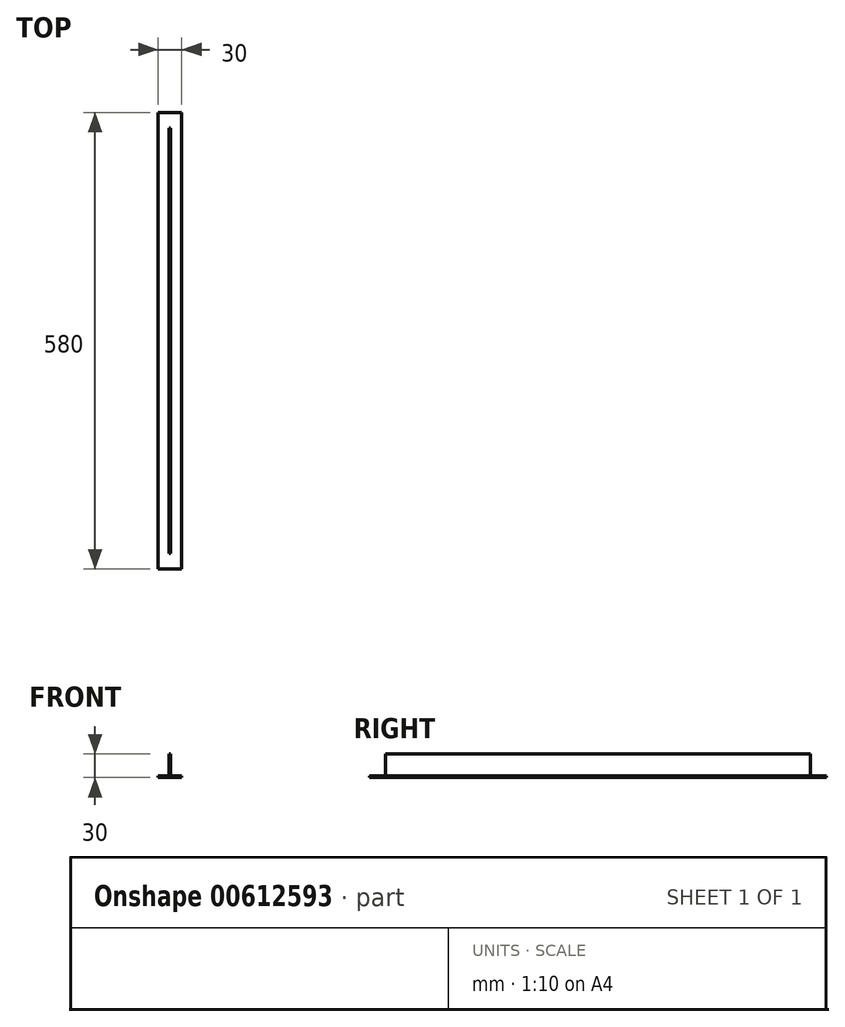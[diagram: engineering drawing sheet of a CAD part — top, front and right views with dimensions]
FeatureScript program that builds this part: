
annotation { "Feature Type Name" : "Feature", "Feature Type Description" : "" }
export const myFeature = defineFeature(function(context is Context, id is Id, definition is map)
    precondition{}
    {
        {
            var Q0;
            Q0=qCreatedBy(makeId("Front.planeOp"),FACE);
            var sketch = newSketch(context, id + "F0", { "sketchPlane" : qUnion([Q0])});
            skLineSegment(sketch, "E0", {"start": v(0, 30) * mm, "end": v(1, 30) * mm});
            skLineSegment(sketch, "E1", {"start": v(1, 30) * mm, "end": v(1, 2) * mm});
            skLineSegment(sketch, "E2", {"start": v(1, 2) * mm, "end": v(15, 2) * mm});
            skLineSegment(sketch, "E3", {"start": v(15, 2) * mm, "end": v(15, 0) * mm});
            skLineSegment(sketch, "E4", {"start": v(15, 0) * mm, "end": v(0, 0) * mm});
            skLineSegment(sketch, "E5", {"start": v(0, 0) * mm, "end": v(0, 30) * mm, "construction": true});
            skLineSegment(sketch, "E6.MirrorCS", {"start": v(0, 30) * mm, "end": v(-1, 30) * mm});
            skLineSegment(sketch, "E7.MirrorCS", {"start": v(-1, 30) * mm, "end": v(-1, 2) * mm});
            skLineSegment(sketch, "E8.MirrorCS", {"start": v(-1, 2) * mm, "end": v(-15, 2) * mm});
            skLineSegment(sketch, "E9.MirrorCS", {"start": v(-15, 2) * mm, "end": v(-15, 0) * mm});
            skLineSegment(sketch, "E10.MirrorCS", {"start": v(-15, 0) * mm, "end": v(0, 0) * mm});
            skSolve(sketch);
        }
        {
            var Q0;
            Q0=makeQuery(id+"F0.imprint","IMPRINT",FACE,{"disambiguationData":[TD([[makeQuery(id+"F0.imprint","IMPRINT",EDGE,{"derivedFrom":sQuery(id+"F0.wireOp",EDGE,"E0")}),-1.0]])]});
            extrude(context, id + "F1", {"entities" : qUnion([Q0]), "depth" : 540 * mm, "offsetDistance" : 25.4 * mm});
        }
        {
            var Q0;
            Q0=makeQuery(id+"F1.opExtrude","CAP_FACE",FACE,{"disambiguationData":[OSD([sQuery(id+"F0.wireOp",EDGE,"E0"),sQuery(id+"F0.wireOp",EDGE,"E1"),sQuery(id+"F0.wireOp",EDGE,"E2"),sQuery(id+"F0.wireOp",EDGE,"E3"),sQuery(id+"F0.wireOp",EDGE,"E4"),sQuery(id+"F0.wireOp",EDGE,"E6.MirrorCS"),sQuery(id+"F0.wireOp",EDGE,"E7.MirrorCS"),sQuery(id+"F0.wireOp",EDGE,"E8.MirrorCS"),sQuery(id+"F0.wireOp",EDGE,"E9.MirrorCS"),sQuery(id+"F0.wireOp",EDGE,"E10.MirrorCS")])],"isStart":false});
            var sketch = newSketch(context, id + "F2", { "sketchPlane" : qUnion([Q0])});
            skLineSegment(sketch, "E11.bottom", {"start": v(-15, 2) * mm, "end": v(15, 2) * mm});
            skLineSegment(sketch, "E11.top", {"start": v(-15, 0) * mm, "end": v(15, 0) * mm});
            skLineSegment(sketch, "E11.left", {"start": v(-15, 2) * mm, "end": v(-15, 0) * mm});
            skLineSegment(sketch, "E11.right", {"start": v(15, 2) * mm, "end": v(15, 0) * mm});
            skSolve(sketch);
        }
        {
            var Q0;
            Q0=makeQuery(id+"F2.imprint","IMPRINT",FACE,{"disambiguationData":[TD([[makeQuery(id+"F2.imprint","IMPRINT",EDGE,{"derivedFrom":sQuery(id+"F2.wireOp",EDGE,"E11.top")}),1.0]])]});
            extrude(context, id + "F3", {"entities" : qUnion([Q0]), "operationType" : NewBodyOperationType.ADD, "depth" : 20 * mm, "offsetDistance" : 25.4 * mm});
        }
        {
            var Q0;
            Q0=makeQuery(id+"F1.opExtrude","CAP_FACE",FACE,{"disambiguationData":[OSD([sQuery(id+"F0.wireOp",EDGE,"E0"),sQuery(id+"F0.wireOp",EDGE,"E1"),sQuery(id+"F0.wireOp",EDGE,"E2"),sQuery(id+"F0.wireOp",EDGE,"E3"),sQuery(id+"F0.wireOp",EDGE,"E4"),sQuery(id+"F0.wireOp",EDGE,"E6.MirrorCS"),sQuery(id+"F0.wireOp",EDGE,"E7.MirrorCS"),sQuery(id+"F0.wireOp",EDGE,"E8.MirrorCS"),sQuery(id+"F0.wireOp",EDGE,"E9.MirrorCS"),sQuery(id+"F0.wireOp",EDGE,"E10.MirrorCS")])],"isStart":true});
            var sketch = newSketch(context, id + "F4", { "sketchPlane" : qUnion([Q0])});
            skLineSegment(sketch, "E12.bottom", {"start": v(-15, 2) * mm, "end": v(15, 2) * mm});
            skLineSegment(sketch, "E12.top", {"start": v(-15, 0) * mm, "end": v(15, 0) * mm});
            skLineSegment(sketch, "E12.left", {"start": v(-15, 2) * mm, "end": v(-15, 0) * mm});
            skLineSegment(sketch, "E12.right", {"start": v(15, 2) * mm, "end": v(15, 0) * mm});
            skSolve(sketch);
        }
        {
            var Q0;
            Q0=makeQuery(id+"F4.imprint","IMPRINT",FACE,{"disambiguationData":[TD([[makeQuery(id+"F4.imprint","IMPRINT",EDGE,{"derivedFrom":sQuery(id+"F4.wireOp",EDGE,"E12.top")}),-1.0]])]});
            extrude(context, id + "F5", {"entities" : qUnion([Q0]), "operationType" : NewBodyOperationType.ADD, "depth" : 20 * mm, "offsetDistance" : 25.4 * mm});
        }
    });
